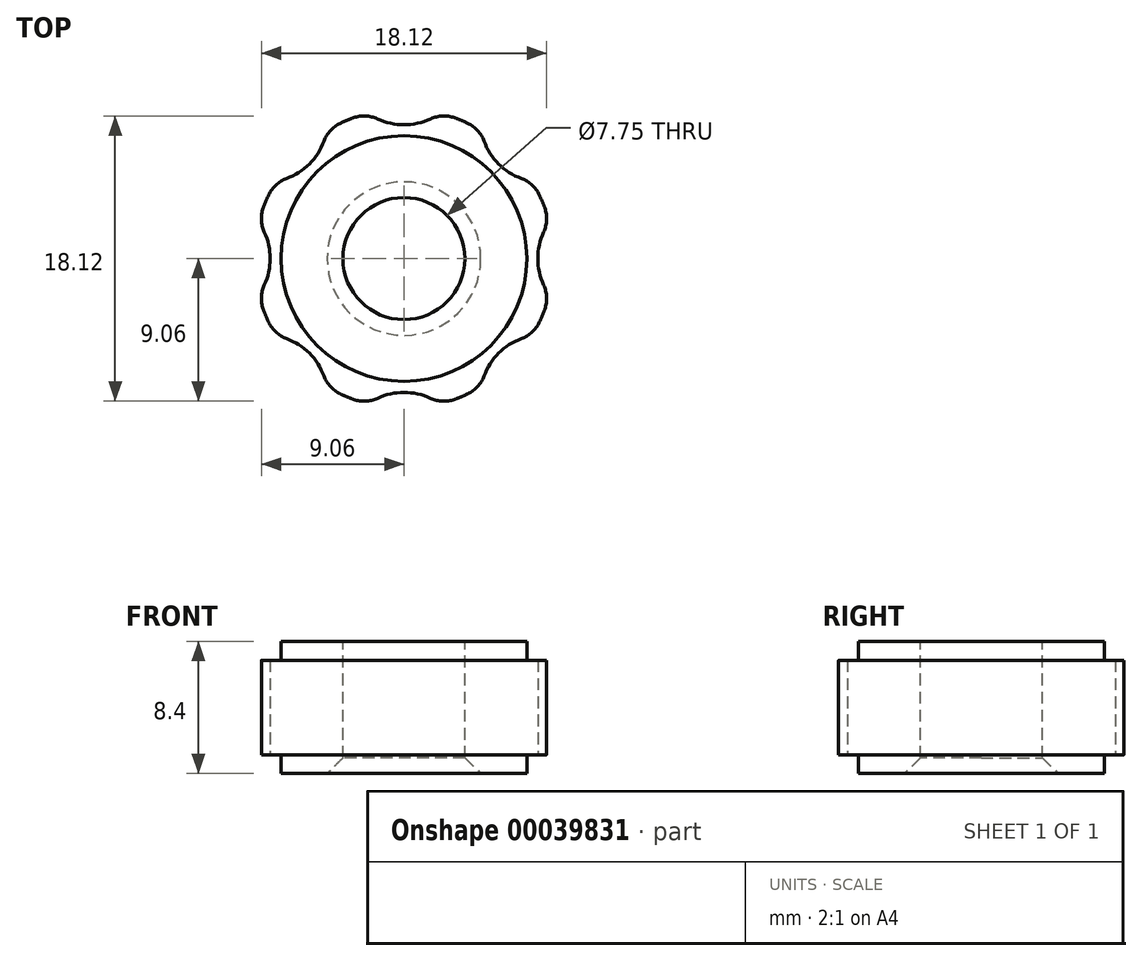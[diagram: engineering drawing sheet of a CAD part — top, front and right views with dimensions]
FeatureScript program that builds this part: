
annotation { "Feature Type Name" : "Feature", "Feature Type Description" : "" }
export const myFeature = defineFeature(function(context is Context, id is Id, definition is map)
    precondition{}
    {
        {
            var Q0;
            Q0=qCreatedBy(makeId("Top.planeOp"),FACE);
            var sketch = newSketch(context, id + "F0", { "sketchPlane" : qUnion([Q0])});
            skCircle(sketch, "E0", {"center": v(0, 0) * mm, "radius": 9.5 * mm});
            skSolve(sketch);
        }
        {
            var Q0;
            Q0=qSketchRegion(id+"F0",true);
            extrude(context, id + "F1", {"entities" : qUnion([Q0]), "depth" : 6 * mm});
        }
        {
            var Q0;
            Q0=makeQuery(id+"F1.opExtrude","CAP_FACE",FACE,{"disambiguationData":[OSD([sQuery(id+"F0.wireOp",EDGE,"E0")])],"isStart":false});
            var sketch = newSketch(context, id + "F2", { "sketchPlane" : qUnion([Q0])});
            skCircle(sketch, "E1", {"center": v(0, 0) * mm, "radius": 7.8 * mm});
            skSolve(sketch);
        }
        {
            var Q0;
            Q0=qSketchRegion(id+"F2",true);
            extrude(context, id + "F3", {"entities" : qUnion([Q0]), "operationType" : NewBodyOperationType.ADD, "depth" : 1.2 * mm});
        }
        {
            var Q0;
            Q0=makeQuery(id+"F1.opExtrude","CAP_FACE",FACE,{"disambiguationData":[OSD([sQuery(id+"F0.wireOp",EDGE,"E0")])],"isStart":true});
            var sketch = newSketch(context, id + "F4", { "sketchPlane" : qUnion([Q0])});
            skCircle(sketch, "E2", {"center": v(0, 0) * mm, "radius": 7.8 * mm});
            skSolve(sketch);
        }
        {
            var Q0;
            Q0=qSketchRegion(id+"F4",true);
            extrude(context, id + "F5", {"entities" : qUnion([Q0]), "operationType" : NewBodyOperationType.ADD, "depth" : 1.2 * mm});
        }
        {
            var Q0;
            Q0=makeQuery(id+"F1.opExtrude","CAP_FACE",FACE,{"disambiguationData":[OSD([sQuery(id+"F0.wireOp",EDGE,"E0")])],"isStart":true});
            var sketch = newSketch(context, id + "F6", { "sketchPlane" : qUnion([Q0])});
            skCircle(sketch, "E3", {"center": v(0, 0) * mm, "radius": 12.5 * mm, "construction": true});
            skCircle(sketch, "E4", {"center": v(0, 12.5) * mm, "radius": 4 * mm});
            skCircle(sketch, "E5.1.0", {"center": v(-8.84, 8.84) * mm, "radius": 4 * mm});
            skCircle(sketch, "E5.2.0", {"center": v(-12.5, 0) * mm, "radius": 4 * mm});
            skCircle(sketch, "E5.3.0", {"center": v(-8.84, -8.84) * mm, "radius": 4 * mm});
            skCircle(sketch, "E5.4.0", {"center": v(0, -12.5) * mm, "radius": 4 * mm});
            skCircle(sketch, "E5.5.0", {"center": v(8.84, -8.84) * mm, "radius": 4 * mm});
            skCircle(sketch, "E5.6.0", {"center": v(12.5, 0) * mm, "radius": 4 * mm});
            skCircle(sketch, "E5.7.0", {"center": v(8.84, 8.84) * mm, "radius": 4 * mm});
            skSolve(sketch);
        }
        {
            var Q0;
            Q0=qSketchRegion(id+"F6",true);
            var Q1;
            Q1=makeQuery(id+"F1.opExtrude","CAP_FACE",FACE,{"disambiguationData":[OSD([sQuery(id+"F0.wireOp",EDGE,"E0")])],"isStart":false});
            extrude(context, id + "F7", {"entities" : qUnion([Q0]), "operationType" : NewBodyOperationType.REMOVE, "endBound" : BoundingType.UP_TO_SURFACE, "oppositeDirection" : true, "endBoundEntityFace" : qUnion([Q1]), "depth" : 25 * mm});
        }
        {
            var Q0;
            Q0=makeQuery(id+"F7.boolean.opBoolean","INTERSECT",EDGE,{"disambiguationData":[OD(0.0)],"derivedFrom":[makeQuery(id+"F1.opExtrude","SWEPT_FACE",FACE,{"disambiguationData":[OSD([sQuery(id+"F0.wireOp",EDGE,"E0")])]}),makeQuery(id+"F7.opExtrude","SWEPT_FACE",FACE,{"disambiguationData":[OSD([sQuery(id+"F6.wireOp",EDGE,"E5.2.0")])]})]});
            var Q1;
            Q1=makeQuery(id+"F7.boolean.opBoolean","INTERSECT",EDGE,{"disambiguationData":[OD(1.0)],"derivedFrom":[makeQuery(id+"F1.opExtrude","SWEPT_FACE",FACE,{"disambiguationData":[OSD([sQuery(id+"F0.wireOp",EDGE,"E0")])]}),makeQuery(id+"F7.opExtrude","SWEPT_FACE",FACE,{"disambiguationData":[OSD([sQuery(id+"F6.wireOp",EDGE,"E5.1.0")])]})]});
            var Q2;
            Q2=makeQuery(id+"F7.boolean.opBoolean","INTERSECT",EDGE,{"disambiguationData":[OD(1.0)],"derivedFrom":[makeQuery(id+"F1.opExtrude","SWEPT_FACE",FACE,{"disambiguationData":[OSD([sQuery(id+"F0.wireOp",EDGE,"E0")])]}),makeQuery(id+"F7.opExtrude","SWEPT_FACE",FACE,{"disambiguationData":[OSD([sQuery(id+"F6.wireOp",EDGE,"E5.2.0")])]})]});
            var Q3;
            Q3=makeQuery(id+"F7.boolean.opBoolean","INTERSECT",EDGE,{"disambiguationData":[OD(0.0)],"derivedFrom":[makeQuery(id+"F1.opExtrude","SWEPT_FACE",FACE,{"disambiguationData":[OSD([sQuery(id+"F0.wireOp",EDGE,"E0")])]}),makeQuery(id+"F7.opExtrude","SWEPT_FACE",FACE,{"disambiguationData":[OSD([sQuery(id+"F6.wireOp",EDGE,"E5.3.0")])]})]});
            var Q4;
            Q4=makeQuery(id+"F7.boolean.opBoolean","INTERSECT",EDGE,{"disambiguationData":[OD(1.0)],"derivedFrom":[makeQuery(id+"F1.opExtrude","SWEPT_FACE",FACE,{"disambiguationData":[OSD([sQuery(id+"F0.wireOp",EDGE,"E0")])]}),makeQuery(id+"F7.opExtrude","SWEPT_FACE",FACE,{"disambiguationData":[OSD([sQuery(id+"F6.wireOp",EDGE,"E5.3.0")])]})]});
            var Q5;
            Q5=makeQuery(id+"F7.boolean.opBoolean","INTERSECT",EDGE,{"disambiguationData":[OD(0.0)],"derivedFrom":[makeQuery(id+"F1.opExtrude","SWEPT_FACE",FACE,{"disambiguationData":[OSD([sQuery(id+"F0.wireOp",EDGE,"E0")])]}),makeQuery(id+"F7.opExtrude","SWEPT_FACE",FACE,{"disambiguationData":[OSD([sQuery(id+"F6.wireOp",EDGE,"E5.4.0")])]})]});
            var Q6;
            Q6=makeQuery(id+"F7.boolean.opBoolean","INTERSECT",EDGE,{"disambiguationData":[OD(1.0)],"derivedFrom":[makeQuery(id+"F1.opExtrude","SWEPT_FACE",FACE,{"disambiguationData":[OSD([sQuery(id+"F0.wireOp",EDGE,"E0")])]}),makeQuery(id+"F7.opExtrude","SWEPT_FACE",FACE,{"disambiguationData":[OSD([sQuery(id+"F6.wireOp",EDGE,"E5.4.0")])]})]});
            var Q7;
            Q7=makeQuery(id+"F7.boolean.opBoolean","INTERSECT",EDGE,{"disambiguationData":[OD(0.0)],"derivedFrom":[makeQuery(id+"F1.opExtrude","SWEPT_FACE",FACE,{"disambiguationData":[OSD([sQuery(id+"F0.wireOp",EDGE,"E0")])]}),makeQuery(id+"F7.opExtrude","SWEPT_FACE",FACE,{"disambiguationData":[OSD([sQuery(id+"F6.wireOp",EDGE,"E5.5.0")])]})]});
            var Q8;
            Q8=makeQuery(id+"F7.boolean.opBoolean","INTERSECT",EDGE,{"disambiguationData":[OD(1.0)],"derivedFrom":[makeQuery(id+"F1.opExtrude","SWEPT_FACE",FACE,{"disambiguationData":[OSD([sQuery(id+"F0.wireOp",EDGE,"E0")])]}),makeQuery(id+"F7.opExtrude","SWEPT_FACE",FACE,{"disambiguationData":[OSD([sQuery(id+"F6.wireOp",EDGE,"E5.5.0")])]})]});
            var Q9;
            Q9=makeQuery(id+"F7.boolean.opBoolean","INTERSECT",EDGE,{"disambiguationData":[OD(0.0)],"derivedFrom":[makeQuery(id+"F1.opExtrude","SWEPT_FACE",FACE,{"disambiguationData":[OSD([sQuery(id+"F0.wireOp",EDGE,"E0")])]}),makeQuery(id+"F7.opExtrude","SWEPT_FACE",FACE,{"disambiguationData":[OSD([sQuery(id+"F6.wireOp",EDGE,"E5.6.0")])]})]});
            var Q10;
            Q10=makeQuery(id+"F7.boolean.opBoolean","INTERSECT",EDGE,{"disambiguationData":[OD(1.0)],"derivedFrom":[makeQuery(id+"F1.opExtrude","SWEPT_FACE",FACE,{"disambiguationData":[OSD([sQuery(id+"F0.wireOp",EDGE,"E0")])]}),makeQuery(id+"F7.opExtrude","SWEPT_FACE",FACE,{"disambiguationData":[OSD([sQuery(id+"F6.wireOp",EDGE,"E5.6.0")])]})]});
            var Q11;
            Q11=makeQuery(id+"F7.boolean.opBoolean","INTERSECT",EDGE,{"disambiguationData":[OD(1.0)],"derivedFrom":[makeQuery(id+"F1.opExtrude","SWEPT_FACE",FACE,{"disambiguationData":[OSD([sQuery(id+"F0.wireOp",EDGE,"E0")])]}),makeQuery(id+"F7.opExtrude","SWEPT_FACE",FACE,{"disambiguationData":[OSD([sQuery(id+"F6.wireOp",EDGE,"E5.7.0")])]})]});
            var Q12;
            Q12=makeQuery(id+"F7.boolean.opBoolean","INTERSECT",EDGE,{"disambiguationData":[OD(0.0)],"derivedFrom":[makeQuery(id+"F1.opExtrude","SWEPT_FACE",FACE,{"disambiguationData":[OSD([sQuery(id+"F0.wireOp",EDGE,"E0")])]}),makeQuery(id+"F7.opExtrude","SWEPT_FACE",FACE,{"disambiguationData":[OSD([sQuery(id+"F6.wireOp",EDGE,"E5.7.0")])]})]});
            var Q13;
            Q13=makeQuery(id+"F7.boolean.opBoolean","INTERSECT",EDGE,{"disambiguationData":[OD(1.0)],"derivedFrom":[makeQuery(id+"F1.opExtrude","SWEPT_FACE",FACE,{"disambiguationData":[OSD([sQuery(id+"F0.wireOp",EDGE,"E0")])]}),makeQuery(id+"F7.opExtrude","SWEPT_FACE",FACE,{"disambiguationData":[OSD([sQuery(id+"F6.wireOp",EDGE,"E4")])]})]});
            var Q14;
            Q14=makeQuery(id+"F7.boolean.opBoolean","INTERSECT",EDGE,{"disambiguationData":[OD(0.0)],"derivedFrom":[makeQuery(id+"F1.opExtrude","SWEPT_FACE",FACE,{"disambiguationData":[OSD([sQuery(id+"F0.wireOp",EDGE,"E0")])]}),makeQuery(id+"F7.opExtrude","SWEPT_FACE",FACE,{"disambiguationData":[OSD([sQuery(id+"F6.wireOp",EDGE,"E4")])]})]});
            var Q15;
            Q15=makeQuery(id+"F7.boolean.opBoolean","INTERSECT",EDGE,{"disambiguationData":[OD(0.0)],"derivedFrom":[makeQuery(id+"F1.opExtrude","SWEPT_FACE",FACE,{"disambiguationData":[OSD([sQuery(id+"F0.wireOp",EDGE,"E0")])]}),makeQuery(id+"F7.opExtrude","SWEPT_FACE",FACE,{"disambiguationData":[OSD([sQuery(id+"F6.wireOp",EDGE,"E5.1.0")])]})]});
            fillet(context, id + "F8", {"entities" : qUnion([Q0, Q1, Q2, Q3, Q4, Q5, Q6, Q7, Q8, Q9, Q10, Q11, Q12, Q13, Q14, Q15]), "radius" : 2 * mm, "tangentPropagation" : true, "allowEdgeOverflow" : false});
        }
        {
            var Q0;
            Q0=makeQuery(id+"F3.opExtrude","CAP_FACE",FACE,{"disambiguationData":[OSD([sQuery(id+"F2.wireOp",EDGE,"E1")])],"isStart":false});
            var sketch = newSketch(context, id + "F9", { "sketchPlane" : qUnion([Q0])});
            skCircle(sketch, "E6", {"center": v(0, 0) * mm, "radius": 3.88 * mm});
            skSolve(sketch);
        }
        {
            var Q0;
            Q0=qSketchRegion(id+"F9",true);
            extrude(context, id + "F10", {"entities" : qUnion([Q0]), "operationType" : NewBodyOperationType.REMOVE, "endBound" : BoundingType.THROUGH_ALL, "oppositeDirection" : true, "depth" : 25 * mm});
        }
        {
            var Q0;
            Q0=makeQuery(id+"F10.boolean.opBoolean","COPY",EDGE,{"derivedFrom":makeQuery(id+"F10.opExtrude","CAP_EDGE",EDGE,{"disambiguationData":[OSD([sQuery(id+"F9.wireOp",EDGE,"E6")])],"isStart":true})});
            var Q1;
            Q1=makeQuery(id+"F10.boolean.opBoolean","INTERSECT",EDGE,{"derivedFrom":[makeQuery(id+"F5.opExtrude","CAP_FACE",FACE,{"disambiguationData":[OSD([sQuery(id+"F4.wireOp",EDGE,"E2")])],"isStart":false}),makeQuery(id+"F10.opExtrude","SWEPT_FACE",FACE,{"disambiguationData":[OSD([sQuery(id+"F9.wireOp",EDGE,"E6")])]})]});
            chamfer(context, id + "F11", {"entities" : qUnion([Q0, Q1]), "width" : 1 * mm, "tangentPropagation" : true});
        }
        {
            var Q0;
            Q0=makeQuery(id+"F3.opExtrude","CAP_FACE",FACE,{"disambiguationData":[OSD([sQuery(id+"F2.wireOp",EDGE,"E1")])],"isStart":false});
            var sketch = newSketch(context, id + "F12", { "sketchPlane" : qUnion([Q0])});
            skCircle(sketch, "E7", {"center": v(0, 0) * mm, "radius": 3.88 * mm});
            skSolve(sketch);
        }
        {
            var Q0;
            Q0=qSketchRegion(id+"F12",true);
            var Q1;
            Q1=qConstructionFilter(qBodyType(qCreatedBy(id+"F12",EDGE),BodyType.WIRE),ConstructionObject.NO);
            extrude(context, id + "F13", {"entities" : qUnion([Q0]), "bodyType" : ExtendedToolBodyType.SURFACE, "surfaceEntities" : qUnion([Q1]), "depth" : 5 * mm, "hasSecondDirection" : true, "secondDirectionOppositeDirection" : true, "secondDirectionDepth" : 12 * mm});
        }
    });
